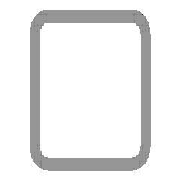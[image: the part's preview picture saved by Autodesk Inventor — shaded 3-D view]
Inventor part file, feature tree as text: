
AUTODESK INVENTOR PART (.ipt)
format: ipt  version: 2022.1 (Build 261234000, 234)  size: 167,424 bytes
history: native  units: mm (DEFAULTED — no unit token found)
features: plane x5, other x4, sketch x4, split x1, extrude x1, boolean_combine x1
ambient origin geometry x8: Origin, YZ Plane, XZ Plane, XY Plane, X Axis, Y Axis, Z Axis, Center Point
bodies: Solid1 (feature_tree), Body (feature_tree), Solid2 (feature_tree)
feature tree (16):
  parser-record x1  (decoder bookkeeping rows leaked as tree rows — omitted from the tree; the rows remain in map.json)
  other  "Driven Length"
  other  "Start Plane"
  other  "End Plane"
  plane  "Work Plane4"
  split  "Split1"
  plane  "Work Plane5"
  plane  "Work Plane6"
  plane  "Work Plane7"
  extrude  "Extrusion2"  TaperAngle=0.0deg  [1 undecoded]
  boolean_combine  "Combine1"
  sketch  "Sketch"  dims[d11=40.0mm d12=2.0mm d13=-0.0mm d14=460.0mm d15=20.0mm d16=20.0mm d17=90.0deg d18=460.0mm d19=0.12mm d20=0.0mm]
  sketch  "Sketch3"  dims[d3=444.0mm d4=0.0mm]
  plane  "Work Plane3"
  sketch  "Sketch4"  dims[d7=4.0mm]
  sketch  "Sketch5"  dims[d9=40.0mm]
note: 1 required parameter value undecoded (feature->parameter linkage not recoverable at this tier; creation-order binding heuristic only, values carry confidence <= 0.55)
